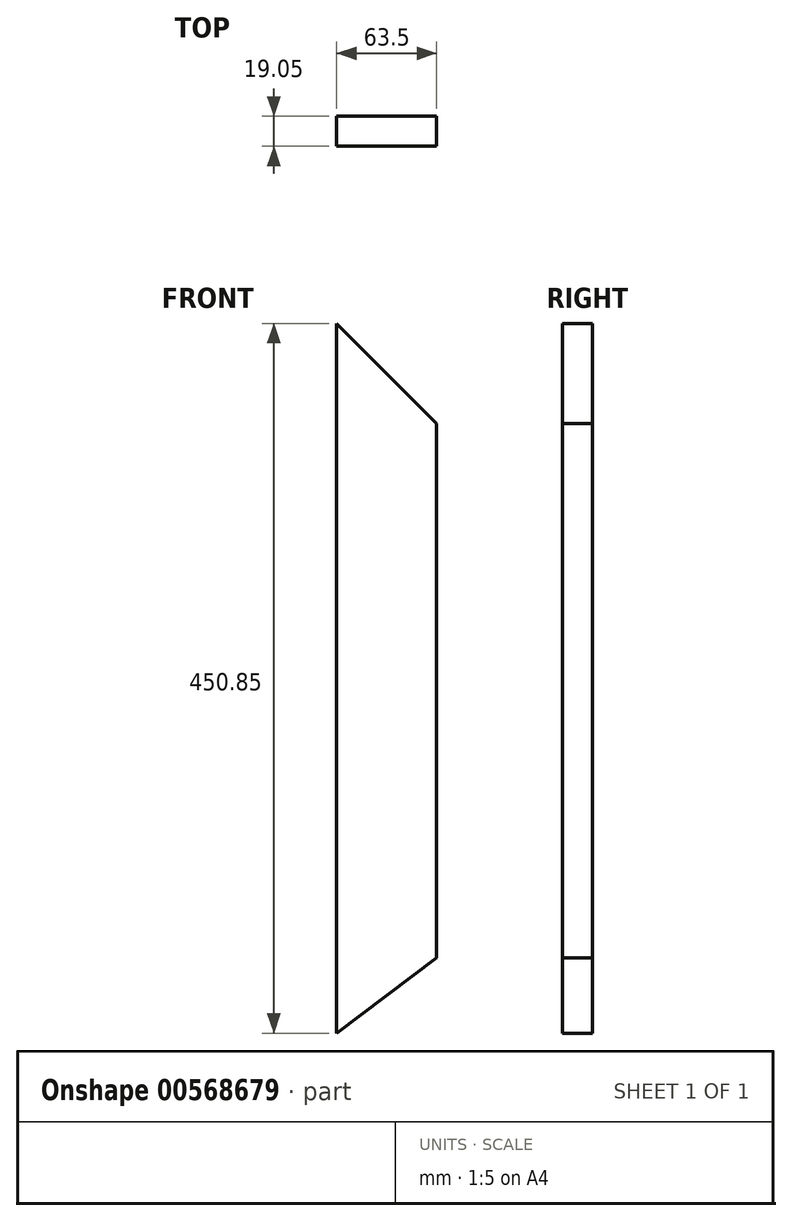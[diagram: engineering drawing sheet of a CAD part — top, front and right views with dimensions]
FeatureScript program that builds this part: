
annotation { "Feature Type Name" : "Feature", "Feature Type Description" : "" }
export const myFeature = defineFeature(function(context is Context, id is Id, definition is map)
    precondition{}
    {
        {
            var Q0;
            Q0=qCreatedBy(makeId("Front.planeOp"),FACE);
            var sketch = newSketch(context, id + "F0", { "sketchPlane" : qUnion([Q0])});
            skLineSegment(sketch, "E0.left", {"start": v(-27.83, 225.42) * mm, "end": v(-27.83, -225.42) * mm});
            skLineSegment(sketch, "E0.right", {"start": v(35.67, 161.92) * mm, "end": v(35.67, -177.6) * mm});
            skPoint(sketch, "E0.middle", {"position": v(0, 0) * mm});
            skLineSegment(sketch, "E1", {"start": v(-27.83, 225.43) * mm, "end": v(35.67, 161.92) * mm});
            skLineSegment(sketch, "E2", {"start": v(-27.83, -225.43) * mm, "end": v(35.67, -177.6) * mm});
            skSolve(sketch);
        }
        {
            var Q0;
            Q0=makeQuery(id+"F0.imprint","IMPRINT",FACE,{"disambiguationData":[TD([[makeQuery(id+"F0.imprint","IMPRINT",EDGE,{"derivedFrom":sQuery(id+"F0.wireOp",EDGE,"E0.left")}),1.0]])]});
            extrude(context, id + "F1", {"entities" : qUnion([Q0]), "depth" : 19.05 * mm, "offsetDistance" : 25.4 * mm});
        }
    });
